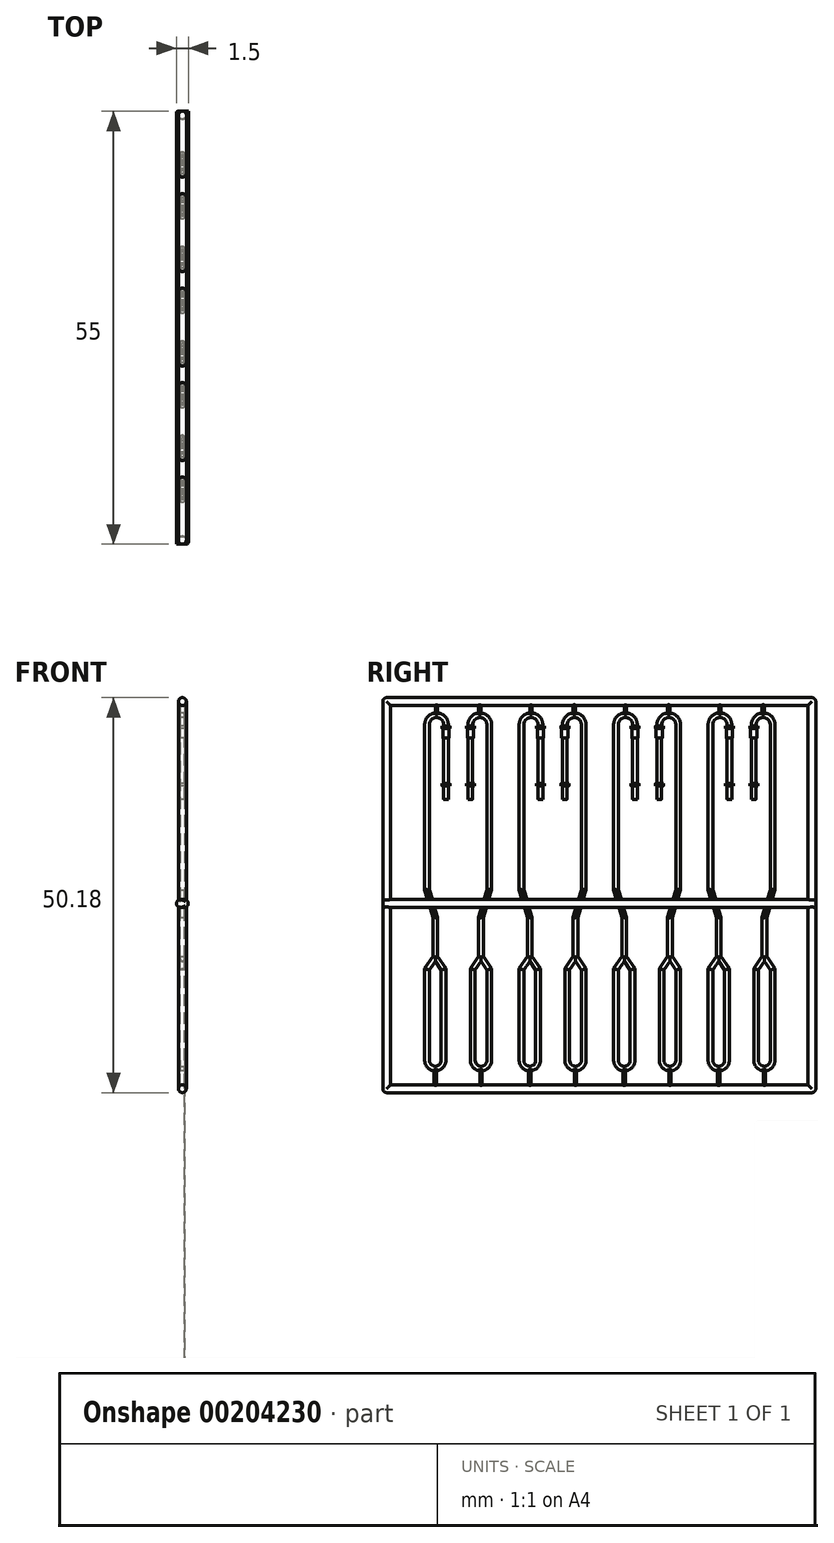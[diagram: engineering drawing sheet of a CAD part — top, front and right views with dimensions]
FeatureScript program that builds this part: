
annotation { "Feature Type Name" : "Feature", "Feature Type Description" : "" }
export const myFeature = defineFeature(function(context is Context, id is Id, definition is map)
    precondition{}
    {
        {
            var Q0;
            Q0=qCreatedBy(makeId("Right.planeOp"),FACE);
            var sketch = newSketch(context, id + "F0", { "sketchPlane" : qUnion([Q0])});
            skLineSegment(sketch, "E0", {"start": v(0, 0) * mm, "end": v(0, 22.5) * mm, "construction": true});
            skLineSegment(sketch, "E1.0", {"start": v(-1.75, 0) * mm, "end": v(-1.75, 21) * mm});
            skLineSegment(sketch, "E2.0", {"start": v(-4.75, 11.5) * mm, "end": v(-4.75, 21) * mm});
            skLineSegment(sketch, "E3", {"start": v(-3.25, 22.5) * mm, "end": v(-3.25, 22.5) * mm});
            skPoint(sketch, "E4.visualSharp", {"position": v(-4.75, 22.5) * mm});
            skArc(sketch, "E4.filletArc", {"start": v(-3.4, 22.5) * mm, "mid": v(-4.36, 22) * mm, "end": v(-4.75, 21) * mm});
            skPoint(sketch, "E5.visualSharp", {"position": v(-1.75, 22.5) * mm});
            skArc(sketch, "E5.filletArc", {"start": v(-1.75, 21) * mm, "mid": v(-2.14, 22) * mm, "end": v(-3.1, 22.5) * mm});
            skLineSegment(sketch, "E6.0", {"start": v(-2.35, 0) * mm, "end": v(-2.35, 21) * mm});
            skArc(sketch, "E6.1", {"start": v(-2.35, 21) * mm, "mid": v(-2.61, 21.64) * mm, "end": v(-3.25, 21.9) * mm});
            skArc(sketch, "E6.2", {"start": v(-3.25, 21.9) * mm, "mid": v(-3.89, 21.64) * mm, "end": v(-4.15, 21) * mm});
            skLineSegment(sketch, "E6.3", {"start": v(-4.15, 11.5) * mm, "end": v(-4.15, 21) * mm});
            skLineSegment(sketch, "E7", {"start": v(-4.75, 11.5) * mm, "end": v(-4.15, 11.5) * mm});
            skLineSegment(sketch, "E8", {"start": v(-2.35, 0) * mm, "end": v(-1.75, 0) * mm});
            skLineSegment(sketch, "E9", {"start": v(0, 0) * mm, "end": v(0, -23) * mm, "construction": true});
            skLineSegment(sketch, "E10.0", {"start": v(-4.45, -10) * mm, "end": v(-4.45, -21.65) * mm});
            skLineSegment(sketch, "E11", {"start": v(-3.1, -23) * mm, "end": v(-3.1, -23) * mm});
            skPoint(sketch, "E12.visualSharp", {"position": v(-4.45, -23) * mm});
            skArc(sketch, "E12.filletArc", {"start": v(-4.45, -21.65) * mm, "mid": v(-4.1, -22.55) * mm, "end": v(-3.25, -23) * mm});
            skPoint(sketch, "E13.visualSharp", {"position": v(-1.75, -23) * mm});
            skArc(sketch, "E13.filletArc", {"start": v(-2.95, -23) * mm, "mid": v(-2.1, -22.55) * mm, "end": v(-1.75, -21.65) * mm});
            skLineSegment(sketch, "E14", {"start": v(-3.1, -9.07) * mm, "end": v(-3.1, -3.5) * mm, "construction": true});
            skLineSegment(sketch, "E15", {"start": v(-4.45, -10) * mm, "end": v(-3.4, -8.44) * mm});
            skLineSegment(sketch, "E16", {"start": v(-2.8, -8.44) * mm, "end": v(-1.75, -10) * mm});
            skLineSegment(sketch, "E17.trimOffspring", {"start": v(-1.75, -10) * mm, "end": v(-1.75, -21.65) * mm});
            skPoint(sketch, "E18.orphan", {"position": v(-3.1, -10) * mm});
            skPoint(sketch, "E19.0.start.orphan", {"position": v(-4.45, -8) * mm});
            skPoint(sketch, "E20.0.end.orphan", {"position": v(-1.75, -8) * mm});
            skLineSegment(sketch, "E21.0", {"start": v(-3.85, -10.18) * mm, "end": v(-3.85, -21.65) * mm});
            skLineSegment(sketch, "E21.1", {"start": v(-3.1, -9.07) * mm, "end": v(-2.35, -10.18) * mm});
            skLineSegment(sketch, "E21.2", {"start": v(-2.35, -10.18) * mm, "end": v(-2.35, -21.65) * mm});
            skLineSegment(sketch, "E21.3", {"start": v(-3.85, -10.18) * mm, "end": v(-3.1, -9.07) * mm});
            skArc(sketch, "E21.4", {"start": v(-3.1, -22.4) * mm, "mid": v(-2.57, -22.18) * mm, "end": v(-2.35, -21.65) * mm});
            skArc(sketch, "E21.5", {"start": v(-3.85, -21.65) * mm, "mid": v(-3.63, -22.18) * mm, "end": v(-3.1, -22.4) * mm});
            skLineSegment(sketch, "E22.0", {"start": v(-2.8, -8.44) * mm, "end": v(-2.8, -3.5) * mm});
            skLineSegment(sketch, "E23.0", {"start": v(-3.4, -8.44) * mm, "end": v(-3.4, -3.5) * mm});
            skLineSegment(sketch, "E24", {"start": v(-3.4, -3.5) * mm, "end": v(-2.8, -3.5) * mm});
            skPoint(sketch, "E25.orphan", {"position": v(-3.1, -8) * mm});
            skLineSegment(sketch, "E26", {"start": v(-2.35, 0) * mm, "end": v(-3.4, -3.5) * mm});
            skLineSegment(sketch, "E27", {"start": v(-1.75, 0) * mm, "end": v(-2.8, -3.5) * mm});
            skLineSegment(sketch, "E28", {"start": v(-3.25, 22.5) * mm, "end": v(-3.25, 24) * mm, "construction": true});
            skLineSegment(sketch, "E29.0", {"start": v(-3.1, 22.5) * mm, "end": v(-3.1, 24) * mm});
            skLineSegment(sketch, "E30.0", {"start": v(-3.4, 22.5) * mm, "end": v(-3.4, 24) * mm});
            skLineSegment(sketch, "E31", {"start": v(-3.4, 24) * mm, "end": v(-3.1, 24) * mm});
            skLineSegment(sketch, "E32", {"start": v(-3.1, -23) * mm, "end": v(-3.1, -25) * mm, "construction": true});
            skLineSegment(sketch, "E33.0", {"start": v(-3.25, -23) * mm, "end": v(-3.25, -25) * mm});
            skLineSegment(sketch, "E34.0", {"start": v(-2.95, -23) * mm, "end": v(-2.95, -25) * mm});
            skLineSegment(sketch, "E35", {"start": v(-3.25, -25) * mm, "end": v(-2.95, -25) * mm});
            skSolve(sketch);
        }
        {
            var Q0;
            Q0 = qSketchRegion(id + "F0", true);
            extrude(context, id + "F1", {"entities" : qUnion([Q0]), "depth" : .3 * mm, "hasSecondDirection" : true, "secondDirectionOppositeDirection" : true, "secondDirectionDepth" : .3 * mm});
        }
        {
            var Q0;
            Q0=makeQuery(id+"F1.opExtrude","CAP_EDGE",EDGE,{"disambiguationData":[OSD([sQuery(id+"F0.wireOp",EDGE,"E2.0")])],"isStart":false});
            var Q1;
            Q1=makeQuery(id+"F1.opExtrude","CAP_EDGE",EDGE,{"disambiguationData":[OSD([sQuery(id+"F0.wireOp",EDGE,"E6.0")])],"isStart":false});
            var Q2;
            Q2=makeQuery(id+"F1.opExtrude","CAP_EDGE",EDGE,{"disambiguationData":[OSD([sQuery(id+"F0.wireOp",EDGE,"E6.0")])],"isStart":true});
            var Q3;
            Q3=makeQuery(id+"F1.opExtrude","CAP_EDGE",EDGE,{"disambiguationData":[OSD([sQuery(id+"F0.wireOp",EDGE,"E2.0")])],"isStart":true});
            var Q4;
            Q4=makeQuery(id+"F1.opExtrude","CAP_EDGE",EDGE,{"disambiguationData":[OSD([sQuery(id+"F0.wireOp",EDGE,"E23.0")])],"isStart":false});
            var Q5;
            Q5=makeQuery(id+"F1.opExtrude","CAP_EDGE",EDGE,{"disambiguationData":[OSD([sQuery(id+"F0.wireOp",EDGE,"E15")])],"isStart":false});
            var Q6;
            Q6=makeQuery(id+"F1.opExtrude","CAP_EDGE",EDGE,{"disambiguationData":[OSD([sQuery(id+"F0.wireOp",EDGE,"E10.0")])],"isStart":false});
            var Q7;
            Q7=makeQuery(id+"F1.opExtrude","CAP_EDGE",EDGE,{"disambiguationData":[OSD([sQuery(id+"F0.wireOp",EDGE,"E23.0")])],"isStart":true});
            var Q8;
            Q8=makeQuery(id+"F1.opExtrude","CAP_EDGE",EDGE,{"disambiguationData":[OSD([sQuery(id+"F0.wireOp",EDGE,"E15")])],"isStart":true});
            var Q9;
            Q9=makeQuery(id+"F1.opExtrude","CAP_EDGE",EDGE,{"disambiguationData":[OSD([sQuery(id+"F0.wireOp",EDGE,"E10.0")])],"isStart":true});
            var Q10;
            Q10=makeQuery(id+"F1.opExtrude","CAP_EDGE",EDGE,{"disambiguationData":[OSD([sQuery(id+"F0.wireOp",EDGE,"E21.2")])],"isStart":true});
            var Q11;
            Q11=makeQuery(id+"F1.opExtrude","CAP_EDGE",EDGE,{"disambiguationData":[OSD([sQuery(id+"F0.wireOp",EDGE,"E21.1")])],"isStart":true});
            var Q12;
            Q12=makeQuery(id+"F1.opExtrude","CAP_EDGE",EDGE,{"disambiguationData":[OSD([sQuery(id+"F0.wireOp",EDGE,"E21.3")])],"isStart":true});
            var Q13;
            Q13=makeQuery(id+"F1.opExtrude","CAP_EDGE",EDGE,{"disambiguationData":[OSD([sQuery(id+"F0.wireOp",EDGE,"E16")])],"isStart":true});
            var Q14;
            Q14=makeQuery(id+"F1.opExtrude","CAP_EDGE",EDGE,{"disambiguationData":[OSD([sQuery(id+"F0.wireOp",EDGE,"E16")])],"isStart":false});
            var Q15;
            Q15=makeQuery(id+"F1.opExtrude","CAP_EDGE",EDGE,{"disambiguationData":[OSD([sQuery(id+"F0.wireOp",EDGE,"E22.0")])],"isStart":true});
            var Q16;
            Q16=makeQuery(id+"F1.opExtrude","CAP_EDGE",EDGE,{"disambiguationData":[OSD([sQuery(id+"F0.wireOp",EDGE,"E22.0")])],"isStart":false});
            var Q17;
            Q17=makeQuery(id+"F1.opExtrude","CAP_EDGE",EDGE,{"disambiguationData":[OSD([sQuery(id+"F0.wireOp",EDGE,"E21.0")])],"isStart":false});
            var Q18;
            Q18=makeQuery(id+"F1.opExtrude","CAP_EDGE",EDGE,{"disambiguationData":[OSD([sQuery(id+"F0.wireOp",EDGE,"E21.3")])],"isStart":false});
            var Q19;
            Q19=makeQuery(id+"F1.opExtrude","CAP_EDGE",EDGE,{"disambiguationData":[OSD([sQuery(id+"F0.wireOp",EDGE,"E21.1")])],"isStart":false});
            var Q20;
            Q20=makeQuery(id+"F1.opExtrude","CAP_EDGE",EDGE,{"disambiguationData":[OSD([sQuery(id+"F0.wireOp",EDGE,"E27")])],"isStart":false});
            var Q21;
            Q21=makeQuery(id+"F1.opExtrude","CAP_EDGE",EDGE,{"disambiguationData":[OSD([sQuery(id+"F0.wireOp",EDGE,"E27")])],"isStart":true});
            var Q22;
            Q22=makeQuery(id+"F1.opExtrude","CAP_EDGE",EDGE,{"disambiguationData":[OSD([sQuery(id+"F0.wireOp",EDGE,"E26")])],"isStart":false});
            var Q23;
            Q23=makeQuery(id+"F1.opExtrude","CAP_EDGE",EDGE,{"disambiguationData":[OSD([sQuery(id+"F0.wireOp",EDGE,"E26")])],"isStart":true});
            var Q24;
            Q24=makeQuery(id+"F1.opExtrude","CAP_EDGE",EDGE,{"disambiguationData":[OSD([sQuery(id+"F0.wireOp",EDGE,"E5.filletArc")])],"isStart":false});
            var Q25;
            Q25=makeQuery(id+"F1.opExtrude","CAP_EDGE",EDGE,{"disambiguationData":[OSD([sQuery(id+"F0.wireOp",EDGE,"E17.trimOffspring")])],"isStart":false});
            var Q26;
            Q26=makeQuery(id+"F1.opExtrude","CAP_EDGE",EDGE,{"disambiguationData":[OSD([sQuery(id+"F0.wireOp",EDGE,"E1.0")])],"isStart":true});
            var Q27;
            Q27=makeQuery(id+"F1.opExtrude","CAP_EDGE",EDGE,{"disambiguationData":[OSD([sQuery(id+"F0.wireOp",EDGE,"E17.trimOffspring")])],"isStart":true});
            fillet(context, id + "F2", {"entities" : qUnion([Q0, Q1, Q2, Q3, Q4, Q5, Q6, Q7, Q8, Q9, Q10, Q11, Q12, Q13, Q14, Q15, Q16, Q17, Q18, Q19, Q20, Q21, Q22, Q23, Q24, Q25, Q26, Q27]), "radius" : .3 * mm, "tangentPropagation" : true, "allowEdgeOverflow" : false});
        }
        {
            var Q0;
            Q0=qCreatedBy(makeId("Top.planeOp"),FACE);
            cPlane(context, id + "F3", {"entities" : qUnion([Q0]), "cplaneType" : CPlaneType.OFFSET, "offset" : 20.8 * mm, "width" : 150 * mm, "height" : 150 * mm});
        }
        {
            var Q0;
            Q0=qCreatedBy(id+"F3.planeOp",FACE);
            var sketch = newSketch(context, id + "F4", { "sketchPlane" : qUnion([Q0])});
            skCircle(sketch, "E36.0", {"center": v(0, -4.45) * mm, "radius": 0.3 * mm, "construction": true});
            skCircle(sketch, "E37", {"center": v(0, -4.45) * mm, "radius": 0.5 * mm});
            skSolve(sketch);
        }
        {
            var Q0;
            Q0 = qSketchRegion(id + "F4", true);
            extrude(context, id + "F5", {"entities" : qUnion([Q0]), "operationType" : NewBodyOperationType.ADD, "oppositeDirection" : true, "depth" : .3 * mm, "offsetDistance" : 25 * mm});
        }
        {
            var Q0;
            Q0=qCreatedBy(id+"F3.planeOp",FACE);
            var sketch = newSketch(context, id + "F6", { "sketchPlane" : qUnion([Q0])});
            skCircle(sketch, "E38.0", {"center": v(0, -4.45) * mm, "radius": 0.3 * mm, "construction": true});
            skCircle(sketch, "E39", {"center": v(0, -4.45) * mm, "radius": 0.4 * mm});
            skSolve(sketch);
        }
        {
            var Q0;
            Q0 = qSketchRegion(id + "F6", true);
            extrude(context, id + "F7", {"entities" : qUnion([Q0]), "operationType" : NewBodyOperationType.ADD, "oppositeDirection" : true, "depth" : 1.5 * mm, "offsetDistance" : 25 * mm});
        }
        {
            var Q0;
            Q0=qCreatedBy(makeId("Top.planeOp"),FACE);
            cPlane(context, id + "F8", {"entities" : qUnion([Q0]), "cplaneType" : CPlaneType.OFFSET, "offset" : 13.5 * mm, "width" : 150 * mm, "height" : 150 * mm});
        }
        {
            var Q0;
            Q0=qCreatedBy(id+"F8.planeOp",FACE);
            var sketch = newSketch(context, id + "F9", { "sketchPlane" : qUnion([Q0])});
            skCircle(sketch, "E40.0", {"center": v(0, -4.45) * mm, "radius": 0.5 * mm});
            skSolve(sketch);
        }
        {
            var Q0;
            Q0 = qSketchRegion(id + "F9", true);
            extrude(context, id + "F10", {"entities" : qUnion([Q0]), "operationType" : NewBodyOperationType.ADD, "oppositeDirection" : true, "depth" : .3 * mm, "offsetDistance" : 25 * mm});
        }
        {
            var Q0;
            Q0=makeQuery(id+"F1.opExtrude","CAP_EDGE",EDGE,{"disambiguationData":[OSD([sQuery(id+"F0.wireOp",EDGE,"E29.0")])],"isStart":false});
            var Q1;
            Q1=makeQuery(id+"F1.opExtrude","CAP_EDGE",EDGE,{"disambiguationData":[OSD([sQuery(id+"F0.wireOp",EDGE,"E30.0")])],"isStart":false});
            var Q2;
            Q2=makeQuery(id+"F1.opExtrude","CAP_EDGE",EDGE,{"disambiguationData":[OSD([sQuery(id+"F0.wireOp",EDGE,"E30.0")])],"isStart":true});
            var Q3;
            Q3=makeQuery(id+"F1.opExtrude","CAP_EDGE",EDGE,{"disambiguationData":[OSD([sQuery(id+"F0.wireOp",EDGE,"E29.0")])],"isStart":true});
            var Q4;
            Q4=makeQuery(id+"F1.opExtrude","CAP_EDGE",EDGE,{"disambiguationData":[OSD([sQuery(id+"F0.wireOp",EDGE,"E34.0")])],"isStart":true});
            var Q5;
            Q5=makeQuery(id+"F1.opExtrude","CAP_EDGE",EDGE,{"disambiguationData":[OSD([sQuery(id+"F0.wireOp",EDGE,"E33.0")])],"isStart":true});
            var Q6;
            Q6=makeQuery(id+"F1.opExtrude","CAP_EDGE",EDGE,{"disambiguationData":[OSD([sQuery(id+"F0.wireOp",EDGE,"E33.0")])],"isStart":false});
            var Q7;
            Q7=makeQuery(id+"F1.opExtrude","CAP_EDGE",EDGE,{"disambiguationData":[OSD([sQuery(id+"F0.wireOp",EDGE,"E34.0")])],"isStart":false});
            fillet(context, id + "F11", {"entities" : qUnion([Q0, Q1, Q2, Q3, Q4, Q5, Q6, Q7]), "radius" : .15 * mm, "tangentPropagation" : true, "allowEdgeOverflow" : false});
        }
        {
            var Q0;
            Q0=makeQuery(id+"F1.opExtrude","SWEPT_BODY",BODY,{"disambiguationData":[OSD([sQuery(id+"F0.wireOp",EDGE,"E1.0"),sQuery(id+"F0.wireOp",EDGE,"E2.0"),sQuery(id+"F0.wireOp",EDGE,"E4.filletArc"),sQuery(id+"F0.wireOp",EDGE,"E5.filletArc"),sQuery(id+"F0.wireOp",EDGE,"E6.0"),sQuery(id+"F0.wireOp",EDGE,"E6.1"),sQuery(id+"F0.wireOp",EDGE,"E6.2"),sQuery(id+"F0.wireOp",EDGE,"E6.3"),sQuery(id+"F0.wireOp",EDGE,"E7"),sQuery(id+"F0.wireOp",EDGE,"E10.0"),sQuery(id+"F0.wireOp",EDGE,"E12.filletArc"),sQuery(id+"F0.wireOp",EDGE,"E13.filletArc"),sQuery(id+"F0.wireOp",EDGE,"E15"),sQuery(id+"F0.wireOp",EDGE,"E16"),sQuery(id+"F0.wireOp",EDGE,"E17.trimOffspring"),sQuery(id+"F0.wireOp",EDGE,"E21.0"),sQuery(id+"F0.wireOp",EDGE,"E21.1"),sQuery(id+"F0.wireOp",EDGE,"E21.2"),sQuery(id+"F0.wireOp",EDGE,"E21.3"),sQuery(id+"F0.wireOp",EDGE,"E21.4"),sQuery(id+"F0.wireOp",EDGE,"E21.5"),sQuery(id+"F0.wireOp",EDGE,"E22.0"),sQuery(id+"F0.wireOp",EDGE,"E23.0"),sQuery(id+"F0.wireOp",EDGE,"E26"),sQuery(id+"F0.wireOp",EDGE,"E27")])]});
            var Q1;
            Q1=qCreatedBy(makeId("Front.planeOp"),FACE);
            mirror(context, id + "F12", {"entities" : qUnion([Q0]), "mirrorPlane" : qUnion([Q1])});
        }
        {
            var Q0;
            Q0=qCreatedBy(makeId("Front.planeOp"),FACE);
            cPlane(context, id + "F13", {"entities" : qUnion([Q0]), "cplaneType" : CPlaneType.OFFSET, "offset" : 6 * mm, "width" : 150 * mm, "height" : 150 * mm});
        }
        {
            var Q0;
            Q0=qCreatedBy(makeId("Front.planeOp"),FACE);
            cPlane(context, id + "F14", {"entities" : qUnion([Q0]), "cplaneType" : CPlaneType.OFFSET, "offset" : 6 * mm, "oppositeDirection" : true, "width" : 150 * mm, "height" : 150 * mm});
        }
        {
            var Q0;
            Q0=makeQuery(id+"F1.opExtrude","SWEPT_BODY",BODY,{"disambiguationData":[OSD([sQuery(id+"F0.wireOp",EDGE,"E1.0"),sQuery(id+"F0.wireOp",EDGE,"E2.0"),sQuery(id+"F0.wireOp",EDGE,"E4.filletArc"),sQuery(id+"F0.wireOp",EDGE,"E5.filletArc"),sQuery(id+"F0.wireOp",EDGE,"E6.0"),sQuery(id+"F0.wireOp",EDGE,"E6.1"),sQuery(id+"F0.wireOp",EDGE,"E6.2"),sQuery(id+"F0.wireOp",EDGE,"E6.3"),sQuery(id+"F0.wireOp",EDGE,"E7"),sQuery(id+"F0.wireOp",EDGE,"E10.0"),sQuery(id+"F0.wireOp",EDGE,"E12.filletArc"),sQuery(id+"F0.wireOp",EDGE,"E13.filletArc"),sQuery(id+"F0.wireOp",EDGE,"E15"),sQuery(id+"F0.wireOp",EDGE,"E16"),sQuery(id+"F0.wireOp",EDGE,"E17.trimOffspring"),sQuery(id+"F0.wireOp",EDGE,"E21.0"),sQuery(id+"F0.wireOp",EDGE,"E21.1"),sQuery(id+"F0.wireOp",EDGE,"E21.2"),sQuery(id+"F0.wireOp",EDGE,"E21.3"),sQuery(id+"F0.wireOp",EDGE,"E21.4"),sQuery(id+"F0.wireOp",EDGE,"E21.5"),sQuery(id+"F0.wireOp",EDGE,"E22.0"),sQuery(id+"F0.wireOp",EDGE,"E23.0"),sQuery(id+"F0.wireOp",EDGE,"E26"),sQuery(id+"F0.wireOp",EDGE,"E27")])]});
            var Q1;
            Q1=qCreatedBy(id+"F13.planeOp",FACE);
            mirror(context, id + "F15", {"entities" : qUnion([Q0]), "mirrorPlane" : qUnion([Q1])});
        }
        {
            var Q0;
            Q0=makeQuery(id+"F12.opPattern","COPY",BODY,{"derivedFrom":makeQuery(id+"F1.opExtrude","SWEPT_BODY",BODY,{"disambiguationData":[OSD([sQuery(id+"F0.wireOp",EDGE,"E1.0"),sQuery(id+"F0.wireOp",EDGE,"E2.0"),sQuery(id+"F0.wireOp",EDGE,"E4.filletArc"),sQuery(id+"F0.wireOp",EDGE,"E5.filletArc"),sQuery(id+"F0.wireOp",EDGE,"E6.0"),sQuery(id+"F0.wireOp",EDGE,"E6.1"),sQuery(id+"F0.wireOp",EDGE,"E6.2"),sQuery(id+"F0.wireOp",EDGE,"E6.3"),sQuery(id+"F0.wireOp",EDGE,"E7"),sQuery(id+"F0.wireOp",EDGE,"E10.0"),sQuery(id+"F0.wireOp",EDGE,"E12.filletArc"),sQuery(id+"F0.wireOp",EDGE,"E13.filletArc"),sQuery(id+"F0.wireOp",EDGE,"E15"),sQuery(id+"F0.wireOp",EDGE,"E16"),sQuery(id+"F0.wireOp",EDGE,"E17.trimOffspring"),sQuery(id+"F0.wireOp",EDGE,"E21.0"),sQuery(id+"F0.wireOp",EDGE,"E21.1"),sQuery(id+"F0.wireOp",EDGE,"E21.2"),sQuery(id+"F0.wireOp",EDGE,"E21.3"),sQuery(id+"F0.wireOp",EDGE,"E21.4"),sQuery(id+"F0.wireOp",EDGE,"E21.5"),sQuery(id+"F0.wireOp",EDGE,"E22.0"),sQuery(id+"F0.wireOp",EDGE,"E23.0"),sQuery(id+"F0.wireOp",EDGE,"E26"),sQuery(id+"F0.wireOp",EDGE,"E27")])]}),"instanceName":"1"});
            var Q1;
            Q1=qCreatedBy(id+"F14.planeOp",FACE);
            mirror(context, id + "F16", {"entities" : qUnion([Q0]), "mirrorPlane" : qUnion([Q1])});
        }
        {
            var Q0;
            Q0=qCreatedBy(makeId("Front.planeOp"),FACE);
            cPlane(context, id + "F17", {"entities" : qUnion([Q0]), "cplaneType" : CPlaneType.OFFSET, "offset" : 12 * mm, "width" : 150 * mm, "height" : 150 * mm});
        }
        {
            var Q0;
            Q0=makeQuery(id+"F1.opExtrude","SWEPT_BODY",BODY,{"disambiguationData":[OSD([sQuery(id+"F0.wireOp",EDGE,"E1.0"),sQuery(id+"F0.wireOp",EDGE,"E2.0"),sQuery(id+"F0.wireOp",EDGE,"E4.filletArc"),sQuery(id+"F0.wireOp",EDGE,"E5.filletArc"),sQuery(id+"F0.wireOp",EDGE,"E6.0"),sQuery(id+"F0.wireOp",EDGE,"E6.1"),sQuery(id+"F0.wireOp",EDGE,"E6.2"),sQuery(id+"F0.wireOp",EDGE,"E6.3"),sQuery(id+"F0.wireOp",EDGE,"E7"),sQuery(id+"F0.wireOp",EDGE,"E10.0"),sQuery(id+"F0.wireOp",EDGE,"E12.filletArc"),sQuery(id+"F0.wireOp",EDGE,"E13.filletArc"),sQuery(id+"F0.wireOp",EDGE,"E15"),sQuery(id+"F0.wireOp",EDGE,"E16"),sQuery(id+"F0.wireOp",EDGE,"E17.trimOffspring"),sQuery(id+"F0.wireOp",EDGE,"E21.0"),sQuery(id+"F0.wireOp",EDGE,"E21.1"),sQuery(id+"F0.wireOp",EDGE,"E21.2"),sQuery(id+"F0.wireOp",EDGE,"E21.3"),sQuery(id+"F0.wireOp",EDGE,"E21.4"),sQuery(id+"F0.wireOp",EDGE,"E21.5"),sQuery(id+"F0.wireOp",EDGE,"E22.0"),sQuery(id+"F0.wireOp",EDGE,"E23.0"),sQuery(id+"F0.wireOp",EDGE,"E26"),sQuery(id+"F0.wireOp",EDGE,"E27")])]});
            var Q1;
            Q1=makeQuery(id+"F12.opPattern","COPY",BODY,{"derivedFrom":makeQuery(id+"F1.opExtrude","SWEPT_BODY",BODY,{"disambiguationData":[OSD([sQuery(id+"F0.wireOp",EDGE,"E1.0"),sQuery(id+"F0.wireOp",EDGE,"E2.0"),sQuery(id+"F0.wireOp",EDGE,"E4.filletArc"),sQuery(id+"F0.wireOp",EDGE,"E5.filletArc"),sQuery(id+"F0.wireOp",EDGE,"E6.0"),sQuery(id+"F0.wireOp",EDGE,"E6.1"),sQuery(id+"F0.wireOp",EDGE,"E6.2"),sQuery(id+"F0.wireOp",EDGE,"E6.3"),sQuery(id+"F0.wireOp",EDGE,"E7"),sQuery(id+"F0.wireOp",EDGE,"E10.0"),sQuery(id+"F0.wireOp",EDGE,"E12.filletArc"),sQuery(id+"F0.wireOp",EDGE,"E13.filletArc"),sQuery(id+"F0.wireOp",EDGE,"E15"),sQuery(id+"F0.wireOp",EDGE,"E16"),sQuery(id+"F0.wireOp",EDGE,"E17.trimOffspring"),sQuery(id+"F0.wireOp",EDGE,"E21.0"),sQuery(id+"F0.wireOp",EDGE,"E21.1"),sQuery(id+"F0.wireOp",EDGE,"E21.2"),sQuery(id+"F0.wireOp",EDGE,"E21.3"),sQuery(id+"F0.wireOp",EDGE,"E21.4"),sQuery(id+"F0.wireOp",EDGE,"E21.5"),sQuery(id+"F0.wireOp",EDGE,"E22.0"),sQuery(id+"F0.wireOp",EDGE,"E23.0"),sQuery(id+"F0.wireOp",EDGE,"E26"),sQuery(id+"F0.wireOp",EDGE,"E27")])]}),"instanceName":"1"});
            var Q2;
            Q2=makeQuery(id+"F15.opPattern","COPY",BODY,{"derivedFrom":makeQuery(id+"F1.opExtrude","SWEPT_BODY",BODY,{"disambiguationData":[OSD([sQuery(id+"F0.wireOp",EDGE,"E1.0"),sQuery(id+"F0.wireOp",EDGE,"E2.0"),sQuery(id+"F0.wireOp",EDGE,"E4.filletArc"),sQuery(id+"F0.wireOp",EDGE,"E5.filletArc"),sQuery(id+"F0.wireOp",EDGE,"E6.0"),sQuery(id+"F0.wireOp",EDGE,"E6.1"),sQuery(id+"F0.wireOp",EDGE,"E6.2"),sQuery(id+"F0.wireOp",EDGE,"E6.3"),sQuery(id+"F0.wireOp",EDGE,"E7"),sQuery(id+"F0.wireOp",EDGE,"E10.0"),sQuery(id+"F0.wireOp",EDGE,"E12.filletArc"),sQuery(id+"F0.wireOp",EDGE,"E13.filletArc"),sQuery(id+"F0.wireOp",EDGE,"E15"),sQuery(id+"F0.wireOp",EDGE,"E16"),sQuery(id+"F0.wireOp",EDGE,"E17.trimOffspring"),sQuery(id+"F0.wireOp",EDGE,"E21.0"),sQuery(id+"F0.wireOp",EDGE,"E21.1"),sQuery(id+"F0.wireOp",EDGE,"E21.2"),sQuery(id+"F0.wireOp",EDGE,"E21.3"),sQuery(id+"F0.wireOp",EDGE,"E21.4"),sQuery(id+"F0.wireOp",EDGE,"E21.5"),sQuery(id+"F0.wireOp",EDGE,"E22.0"),sQuery(id+"F0.wireOp",EDGE,"E23.0"),sQuery(id+"F0.wireOp",EDGE,"E26"),sQuery(id+"F0.wireOp",EDGE,"E27")])]}),"instanceName":"1"});
            var Q3;
            Q3=makeQuery(id+"F16.opPattern","COPY",BODY,{"derivedFrom":makeQuery(id+"F12.opPattern","COPY",BODY,{"derivedFrom":makeQuery(id+"F1.opExtrude","SWEPT_BODY",BODY,{"disambiguationData":[OSD([sQuery(id+"F0.wireOp",EDGE,"E1.0"),sQuery(id+"F0.wireOp",EDGE,"E2.0"),sQuery(id+"F0.wireOp",EDGE,"E4.filletArc"),sQuery(id+"F0.wireOp",EDGE,"E5.filletArc"),sQuery(id+"F0.wireOp",EDGE,"E6.0"),sQuery(id+"F0.wireOp",EDGE,"E6.1"),sQuery(id+"F0.wireOp",EDGE,"E6.2"),sQuery(id+"F0.wireOp",EDGE,"E6.3"),sQuery(id+"F0.wireOp",EDGE,"E7"),sQuery(id+"F0.wireOp",EDGE,"E10.0"),sQuery(id+"F0.wireOp",EDGE,"E12.filletArc"),sQuery(id+"F0.wireOp",EDGE,"E13.filletArc"),sQuery(id+"F0.wireOp",EDGE,"E15"),sQuery(id+"F0.wireOp",EDGE,"E16"),sQuery(id+"F0.wireOp",EDGE,"E17.trimOffspring"),sQuery(id+"F0.wireOp",EDGE,"E21.0"),sQuery(id+"F0.wireOp",EDGE,"E21.1"),sQuery(id+"F0.wireOp",EDGE,"E21.2"),sQuery(id+"F0.wireOp",EDGE,"E21.3"),sQuery(id+"F0.wireOp",EDGE,"E21.4"),sQuery(id+"F0.wireOp",EDGE,"E21.5"),sQuery(id+"F0.wireOp",EDGE,"E22.0"),sQuery(id+"F0.wireOp",EDGE,"E23.0"),sQuery(id+"F0.wireOp",EDGE,"E26"),sQuery(id+"F0.wireOp",EDGE,"E27")])]}),"instanceName":"1"}),"instanceName":"1"});
            var Q4;
            Q4=qCreatedBy(id+"F17.planeOp",FACE);
            mirror(context, id + "F18", {"entities" : qUnion([Q0, Q1, Q2, Q3]), "mirrorPlane" : qUnion([Q4])});
        }
        {
            var Q0;
            Q0=qCreatedBy(makeId("Right.planeOp"),FACE);
            var sketch = newSketch(context, id + "F19", { "sketchPlane" : qUnion([Q0])});
            skLineSegment(sketch, "E41", {"start": v(-39.58, -1.24) * mm, "end": v(15.42, -1.24) * mm});
            skLineSegment(sketch, "E42", {"start": v(15.42, -1.24) * mm, "end": v(15.42, -2.24) * mm});
            skLineSegment(sketch, "E43", {"start": v(15.42, -2.24) * mm, "end": v(-39.58, -2.24) * mm});
            skLineSegment(sketch, "E44.0", {"start": v(-39.58, -1.24) * mm, "end": v(-39.58, -2.24) * mm});
            skSolve(sketch);
        }
        {
            var Q0;
            Q0 = qSketchRegion(id + "F19", true);
            extrude(context, id + "F20", {"entities" : qUnion([Q0]), "operationType" : NewBodyOperationType.ADD, "depth" : .75 * mm, "hasSecondDirection" : true, "secondDirectionOppositeDirection" : true, "secondDirectionDepth" : .75 * mm});
        }
        {
            var Q0;
            Q0=qCreatedBy(makeId("Right.planeOp"),FACE);
            var sketch = newSketch(context, id + "F21", { "sketchPlane" : qUnion([Q0])});
            skLineSegment(sketch, "E45.0", {"start": v(-39.58, 24.42) * mm, "end": v(-39.58, -25.76) * mm});
            skLineSegment(sketch, "E46.0", {"start": v(15.42, 24.42) * mm, "end": v(15.42, -25.76) * mm});
            skPoint(sketch, "E47.orphan", {"position": v(15.42, -1.24) * mm});
            skLineSegment(sketch, "E48", {"start": v(-38.58, 23.42) * mm, "end": v(14.42, 23.42) * mm});
            skLineSegment(sketch, "E49.0", {"start": v(-39.58, 24.42) * mm, "end": v(15.42, 24.42) * mm});
            skLineSegment(sketch, "E50.0", {"start": v(-38.58, 23.42) * mm, "end": v(-38.58, -24.76) * mm});
            skLineSegment(sketch, "E51.0", {"start": v(14.42, 23.42) * mm, "end": v(14.42, -24.76) * mm});
            skPoint(sketch, "E52.orphan", {"position": v(15.42, -2.24) * mm});
            skLineSegment(sketch, "E53.0", {"start": v(15.42, -25.76) * mm, "end": v(-39.58, -25.76) * mm});
            skLineSegment(sketch, "E54.trimOffspring", {"start": v(14.42, -24.76) * mm, "end": v(-38.58, -24.76) * mm});
            skPoint(sketch, "E55.orphan", {"position": v(-39.58, -1.24) * mm});
            skSolve(sketch);
        }
        {
            var Q0;
            Q0 = qSketchRegion(id + "F21", true);
            extrude(context, id + "F22", {"entities" : qUnion([Q0]), "operationType" : NewBodyOperationType.ADD, "depth" : .5 * mm, "hasSecondDirection" : true, "secondDirectionOppositeDirection" : true, "secondDirectionDepth" : .5 * mm});
        }
        {
            var Q0;
            Q0=makeQuery(id+"F22.opExtrude","CAP_EDGE",EDGE,{"disambiguationData":[OSD([sQuery(id+"F21.wireOp",EDGE,"E49.0")])],"isStart":false});
            var Q1;
            Q1=makeQuery(id+"F22.opExtrude","CAP_EDGE",EDGE,{"disambiguationData":[OSD([sQuery(id+"F21.wireOp",EDGE,"E48")])],"isStart":false});
            var Q2;
            Q2=makeQuery(id+"F20.opExtrude","CAP_EDGE",EDGE,{"disambiguationData":[OSD([sQuery(id+"F19.wireOp",EDGE,"E41")])],"isStart":false});
            var Q3;
            Q3=makeQuery(id+"F20.opExtrude","CAP_EDGE",EDGE,{"disambiguationData":[OSD([sQuery(id+"F19.wireOp",EDGE,"E43")])],"isStart":false});
            var Q4;
            Q4=makeQuery(id+"F22.opExtrude","CAP_EDGE",EDGE,{"disambiguationData":[OSD([sQuery(id+"F21.wireOp",EDGE,"E54.trimOffspring")])],"isStart":false});
            var Q5;
            Q5=makeQuery(id+"F22.opExtrude","CAP_EDGE",EDGE,{"disambiguationData":[OSD([sQuery(id+"F21.wireOp",EDGE,"E53.0")])],"isStart":false});
            var Q6;
            Q6=makeQuery(id+"F22.opExtrude","CAP_EDGE",EDGE,{"disambiguationData":[OSD([sQuery(id+"F21.wireOp",EDGE,"E49.0")])],"isStart":true});
            var Q7;
            Q7=makeQuery(id+"F22.opExtrude","CAP_EDGE",EDGE,{"disambiguationData":[OSD([sQuery(id+"F21.wireOp",EDGE,"E48")])],"isStart":true});
            var Q8;
            Q8=makeQuery(id+"F20.opExtrude","CAP_EDGE",EDGE,{"disambiguationData":[OSD([sQuery(id+"F19.wireOp",EDGE,"E41")])],"isStart":true});
            var Q9;
            Q9=makeQuery(id+"F20.opExtrude","CAP_EDGE",EDGE,{"disambiguationData":[OSD([sQuery(id+"F19.wireOp",EDGE,"E43")])],"isStart":true});
            var Q10;
            Q10=makeQuery(id+"F22.opExtrude","CAP_EDGE",EDGE,{"disambiguationData":[OSD([sQuery(id+"F21.wireOp",EDGE,"E54.trimOffspring")])],"isStart":true});
            var Q11;
            Q11=makeQuery(id+"F22.opExtrude","CAP_EDGE",EDGE,{"disambiguationData":[OSD([sQuery(id+"F21.wireOp",EDGE,"E53.0")])],"isStart":true});
            fillet(context, id + "F23", {"entities" : qUnion([Q0, Q1, Q2, Q3, Q4, Q5, Q6, Q7, Q8, Q9, Q10, Q11]), "radius" : .5 * mm, "tangentPropagation" : true, "allowEdgeOverflow" : false});
        }
        {
            var Q0;
            {var subQ1=sQuery(id+"F21.wireOp",EDGE,"E45.0");Q0=makeQuery(id+"F22.boolean.opBoolean","SPLIT",EDGE,{"disambiguationData":[TD([makeQuery(id+"F20.opExtrude","SWEPT_FACE",FACE,{"disambiguationData":[OSD([sQuery(id+"F19.wireOp",EDGE,"E43")])]})])],"derivedFrom":makeQuery(id+"F22.opExtrude","CAP_EDGE",EDGE,{"disambiguationData":[OSD([subQ1])],"isStart":false})});}
            var Q1;
            {var subQ1=sQuery(id+"F21.wireOp",EDGE,"E45.0");Q1=makeQuery(id+"F22.boolean.opBoolean","SPLIT",EDGE,{"disambiguationData":[TD([makeQuery(id+"F20.opExtrude","SWEPT_FACE",FACE,{"disambiguationData":[OSD([sQuery(id+"F19.wireOp",EDGE,"E41")])]})])],"derivedFrom":makeQuery(id+"F22.opExtrude","CAP_EDGE",EDGE,{"disambiguationData":[OSD([subQ1])],"isStart":false})});}
            var Q2;
            {var subQ0=sQuery(id+"F21.wireOp",EDGE,"E51.0");Q2=makeQuery(id+"F22.boolean.opBoolean","SPLIT",EDGE,{"disambiguationData":[TD([makeQuery(id+"F20.opExtrude","SWEPT_FACE",FACE,{"disambiguationData":[OSD([sQuery(id+"F19.wireOp",EDGE,"E41")])]})])],"derivedFrom":makeQuery(id+"F22.opExtrude","CAP_EDGE",EDGE,{"disambiguationData":[OSD([subQ0])],"isStart":false})});}
            var Q3;
            {var subQ0=sQuery(id+"F21.wireOp",EDGE,"E51.0");Q3=makeQuery(id+"F22.boolean.opBoolean","SPLIT",EDGE,{"disambiguationData":[TD([makeQuery(id+"F20.opExtrude","SWEPT_FACE",FACE,{"disambiguationData":[OSD([sQuery(id+"F19.wireOp",EDGE,"E41")])]})])],"derivedFrom":makeQuery(id+"F22.opExtrude","CAP_EDGE",EDGE,{"disambiguationData":[OSD([subQ0])],"isStart":true})});}
            var Q4;
            {var subQ1=sQuery(id+"F21.wireOp",EDGE,"E51.0");Q4=makeQuery(id+"F22.boolean.opBoolean","SPLIT",EDGE,{"disambiguationData":[TD([makeQuery(id+"F20.opExtrude","SWEPT_FACE",FACE,{"disambiguationData":[OSD([sQuery(id+"F19.wireOp",EDGE,"E43")])]})])],"derivedFrom":makeQuery(id+"F22.opExtrude","CAP_EDGE",EDGE,{"disambiguationData":[OSD([subQ1])],"isStart":false})});}
            var Q5;
            {var subQ1=sQuery(id+"F21.wireOp",EDGE,"E51.0");Q5=makeQuery(id+"F22.boolean.opBoolean","SPLIT",EDGE,{"disambiguationData":[TD([makeQuery(id+"F20.opExtrude","SWEPT_FACE",FACE,{"disambiguationData":[OSD([sQuery(id+"F19.wireOp",EDGE,"E43")])]})])],"derivedFrom":makeQuery(id+"F22.opExtrude","CAP_EDGE",EDGE,{"disambiguationData":[OSD([subQ1])],"isStart":true})});}
            var Q6;
            {var subQ0=sQuery(id+"F21.wireOp",EDGE,"E50.0");Q6=makeQuery(id+"F22.boolean.opBoolean","SPLIT",EDGE,{"disambiguationData":[TD([makeQuery(id+"F20.opExtrude","SWEPT_FACE",FACE,{"disambiguationData":[OSD([sQuery(id+"F19.wireOp",EDGE,"E43")])]})])],"derivedFrom":makeQuery(id+"F22.opExtrude","CAP_EDGE",EDGE,{"disambiguationData":[OSD([subQ0])],"isStart":true})});}
            var Q7;
            {var subQ1=sQuery(id+"F21.wireOp",EDGE,"E50.0");Q7=makeQuery(id+"F22.boolean.opBoolean","SPLIT",EDGE,{"disambiguationData":[TD([makeQuery(id+"F20.opExtrude","SWEPT_FACE",FACE,{"disambiguationData":[OSD([sQuery(id+"F19.wireOp",EDGE,"E43")])]})])],"derivedFrom":makeQuery(id+"F22.opExtrude","CAP_EDGE",EDGE,{"disambiguationData":[OSD([subQ1])],"isStart":false})});}
            var Q8;
            {var subQ0=sQuery(id+"F21.wireOp",EDGE,"E50.0");Q8=makeQuery(id+"F22.boolean.opBoolean","SPLIT",EDGE,{"disambiguationData":[TD([makeQuery(id+"F20.opExtrude","SWEPT_FACE",FACE,{"disambiguationData":[OSD([sQuery(id+"F19.wireOp",EDGE,"E41")])]})])],"derivedFrom":makeQuery(id+"F22.opExtrude","CAP_EDGE",EDGE,{"disambiguationData":[OSD([subQ0])],"isStart":false})});}
            var Q9;
            {var subQ0=sQuery(id+"F21.wireOp",EDGE,"E50.0");Q9=makeQuery(id+"F22.boolean.opBoolean","SPLIT",EDGE,{"disambiguationData":[TD([makeQuery(id+"F20.opExtrude","SWEPT_FACE",FACE,{"disambiguationData":[OSD([sQuery(id+"F19.wireOp",EDGE,"E41")])]})])],"derivedFrom":makeQuery(id+"F22.opExtrude","CAP_EDGE",EDGE,{"disambiguationData":[OSD([subQ0])],"isStart":true})});}
            var Q10;
            {var subQ1=sQuery(id+"F21.wireOp",EDGE,"E46.0");Q10=makeQuery(id+"F22.boolean.opBoolean","SPLIT",EDGE,{"disambiguationData":[TD([makeQuery(id+"F20.opExtrude","SWEPT_FACE",FACE,{"disambiguationData":[OSD([sQuery(id+"F19.wireOp",EDGE,"E41")])]})])],"derivedFrom":makeQuery(id+"F22.opExtrude","CAP_EDGE",EDGE,{"disambiguationData":[OSD([subQ1])],"isStart":false})});}
            var Q11;
            {var subQ0=sQuery(id+"F21.wireOp",EDGE,"E46.0");Q11=makeQuery(id+"F22.boolean.opBoolean","SPLIT",EDGE,{"disambiguationData":[TD([makeQuery(id+"F20.opExtrude","SWEPT_FACE",FACE,{"disambiguationData":[OSD([sQuery(id+"F19.wireOp",EDGE,"E43")])]})])],"derivedFrom":makeQuery(id+"F22.opExtrude","CAP_EDGE",EDGE,{"disambiguationData":[OSD([subQ0])],"isStart":false})});}
            fillet(context, id + "F24", {"entities" : qUnion([Q0, Q1, Q2, Q3, Q4, Q5, Q6, Q7, Q8, Q9, Q10, Q11]), "radius" : .5 * mm, "tangentPropagation" : true, "allowEdgeOverflow" : false});
        }
        {
            var Q0;
            Q0=makeQuery(id+"F23.opFillet","BLEND_EDGE",EDGE,{"blendedFrom":[makeQuery(id+"F20.opExtrude","CAP_EDGE",EDGE,{"disambiguationData":[OSD([sQuery(id+"F19.wireOp",EDGE,"E41")])],"isStart":true}),makeQuery(id+"F22.boolean.opBoolean","MERGE",FACE,{"derivedFrom":[makeQuery(id+"F20.opExtrude","SWEPT_FACE",FACE,{"disambiguationData":[OSD([sQuery(id+"F19.wireOp",EDGE,"E42")])]}),makeQuery(id+"F22.opExtrude","SWEPT_FACE",FACE,{"disambiguationData":[OSD([sQuery(id+"F21.wireOp",EDGE,"E46.0")])]})]})],"blendedInto":[makeQuery(id+"F22.boolean.opBoolean","MERGE",FACE,{"derivedFrom":[makeQuery(id+"F20.opExtrude","SWEPT_FACE",FACE,{"disambiguationData":[OSD([sQuery(id+"F19.wireOp",EDGE,"E42")])]}),makeQuery(id+"F22.opExtrude","SWEPT_FACE",FACE,{"disambiguationData":[OSD([sQuery(id+"F21.wireOp",EDGE,"E46.0")])]})]})]});
            var Q1;
            Q1=makeQuery(id+"F23.opFillet","BLEND_EDGE",EDGE,{"blendedFrom":[makeQuery(id+"F20.opExtrude","CAP_EDGE",EDGE,{"disambiguationData":[OSD([sQuery(id+"F19.wireOp",EDGE,"E41")])],"isStart":false}),makeQuery(id+"F22.boolean.opBoolean","MERGE",FACE,{"derivedFrom":[makeQuery(id+"F20.opExtrude","SWEPT_FACE",FACE,{"disambiguationData":[OSD([sQuery(id+"F19.wireOp",EDGE,"E44.0")])]}),makeQuery(id+"F22.opExtrude","SWEPT_FACE",FACE,{"disambiguationData":[OSD([sQuery(id+"F21.wireOp",EDGE,"E45.0")])]})]})],"blendedInto":[makeQuery(id+"F22.boolean.opBoolean","MERGE",FACE,{"derivedFrom":[makeQuery(id+"F20.opExtrude","SWEPT_FACE",FACE,{"disambiguationData":[OSD([sQuery(id+"F19.wireOp",EDGE,"E44.0")])]}),makeQuery(id+"F22.opExtrude","SWEPT_FACE",FACE,{"disambiguationData":[OSD([sQuery(id+"F21.wireOp",EDGE,"E45.0")])]})]})]});
            fillet(context, id + "F25", {"entities" : qUnion([Q0, Q1]), "radius" : .2 * mm, "tangentPropagation" : true, "allowEdgeOverflow" : false});
        }
    });
